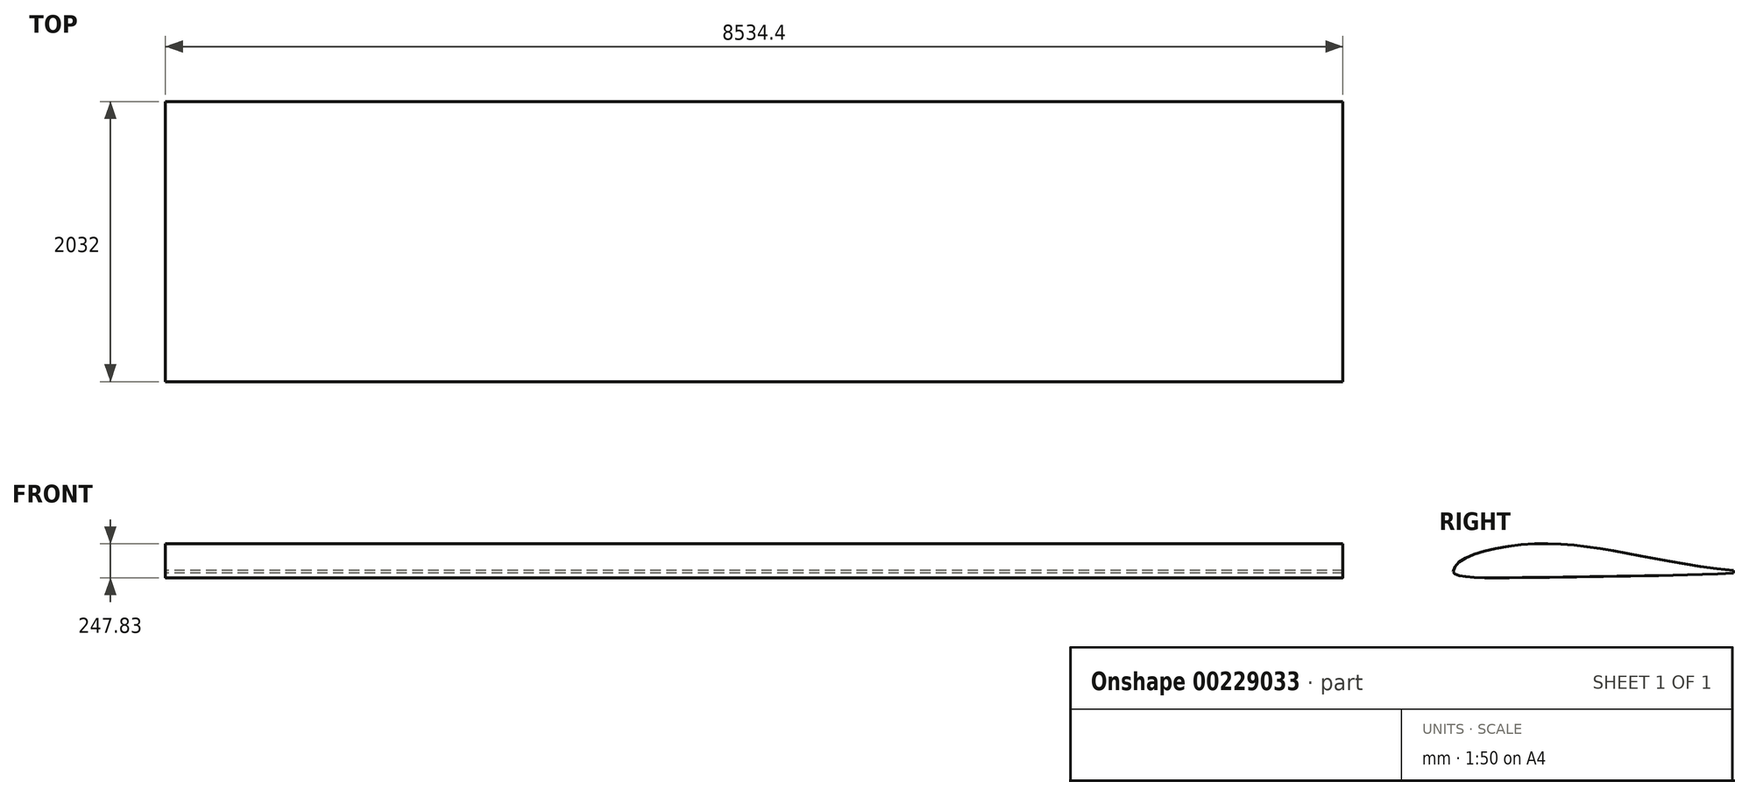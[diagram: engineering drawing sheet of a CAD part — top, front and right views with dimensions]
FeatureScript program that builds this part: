
annotation { "Feature Type Name" : "Feature", "Feature Type Description" : "" }
export const myFeature = defineFeature(function(context is Context, id is Id, definition is map)
    precondition{}
    {
        {
            assignVariable(context, id + "F0", {"name" : "span", "anyValue" : 8534.4 * mm});
        }
        {
            var Q0;
            Q0=qCreatedBy(makeId("Right.planeOp"),FACE);
            var sketch = newSketch(context, id + "F1", { "sketchPlane" : qUnion([Q0])});
            skLineSegment(sketch, "E0", {"start": v(0, 0) * mm, "end": v(2032, 0) * mm, "construction": true});
            skLineSegment(sketch, "E1", {"start": v(609.6, 203.2) * mm, "end": v(609.6, -40.64) * mm, "construction": true});
            skFitSpline(sketch, "E2", {"points": [v(0, 0) * mm, v(609.6, 203.2) * mm, v(2032, 10.16) * mm], "startDerivative": vector(0, 848.32) * mm, "endDerivative": vector(2899.96, -273.37) * mm});
            skLineSegment(sketch, "E3", {"start": v(0, 0) * mm, "end": v(0, 508) * mm, "construction": true});
            skFitSpline(sketch, "E4", {"points": [v(0, 0) * mm, v(609.6, -40.64) * mm, v(2032, -10.16) * mm], "startDerivative": vector(0, -399.08) * mm, "endDerivative": vector(2666.2, 111.15) * mm});
            skLineSegment(sketch, "E5", {"start": v(2032, 10.16) * mm, "end": v(2032, -10.16) * mm});
            skSolve(sketch);
        }
        {
            var Q0;
            Q0=makeQuery(id+"F1.imprint","IMPRINT",FACE,{"disambiguationData":[TD([[makeQuery(id+"F1.imprint","IMPRINT",EDGE,{"derivedFrom":sQuery(id+"F1.wireOp",EDGE,"E2")}),-1.0]])]});
            extrude(context, id + "F2", {"entities" : qUnion([Q0]), "endBound" : BoundingType.SYMMETRIC, "depth" : getVariable(context, 'span')});
        }
    });
